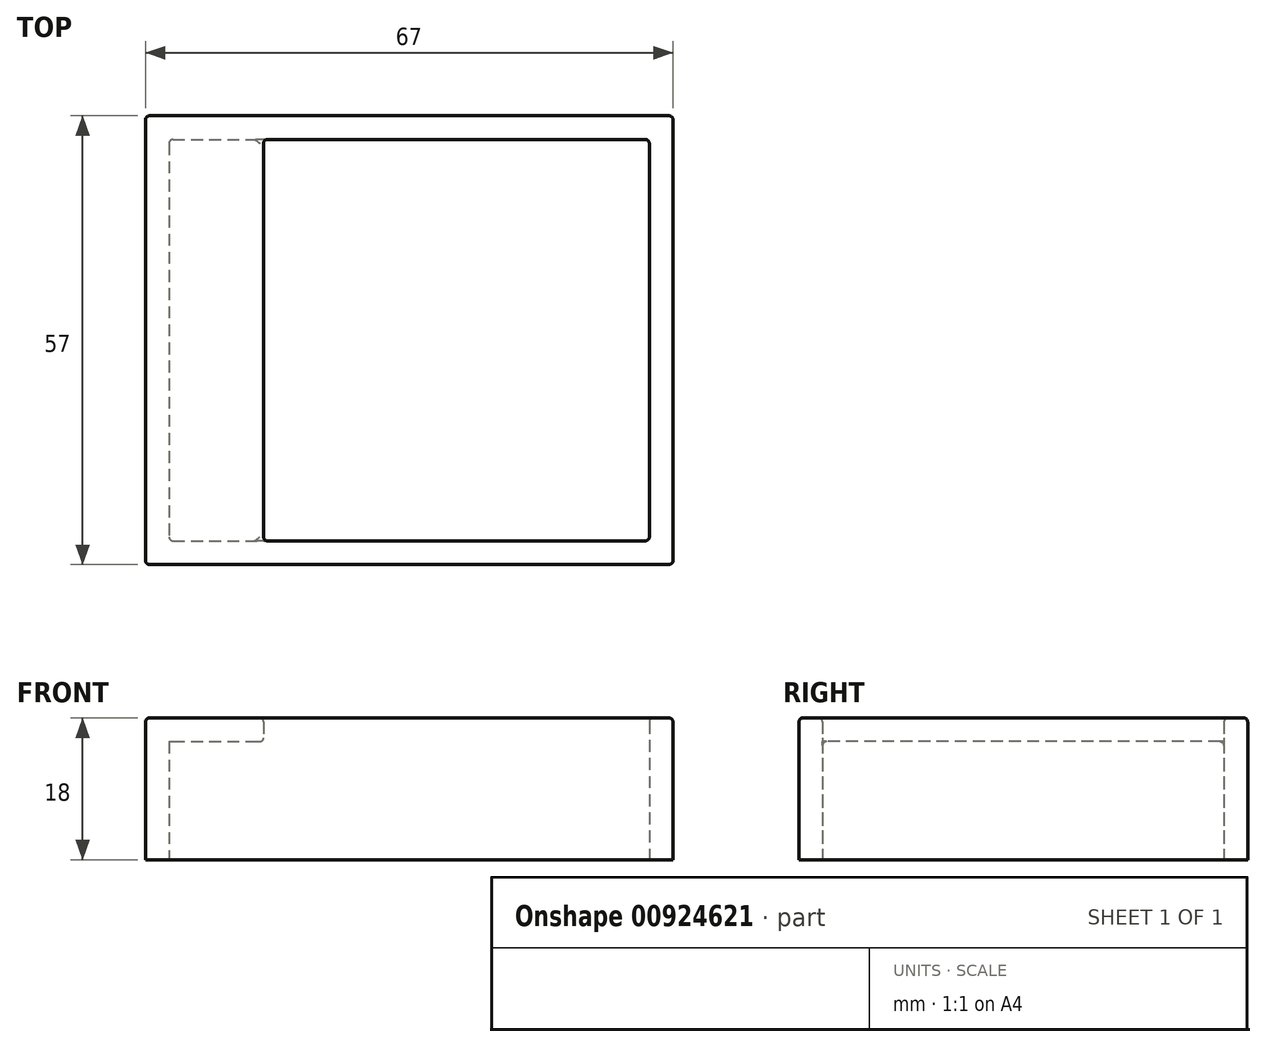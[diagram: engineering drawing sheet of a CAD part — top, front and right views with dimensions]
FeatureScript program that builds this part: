
annotation { "Feature Type Name" : "Feature", "Feature Type Description" : "" }
export const myFeature = defineFeature(function(context is Context, id is Id, definition is map)
    precondition{}
    {
        {
            var Q0;
            Q0=qCreatedBy(makeId("Top.planeOp"),FACE);
            var sketch = newSketch(context, id + "F0", { "sketchPlane" : qUnion([Q0])});
            skLineSegment(sketch, "E0.bottom", {"start": v(-27.46, 16.96) * mm, "end": v(32.54, 16.96) * mm});
            skLineSegment(sketch, "E0.top", {"start": v(-27.46, -34.04) * mm, "end": v(32.54, -34.04) * mm});
            skLineSegment(sketch, "E0.left", {"start": v(-27.96, 16.46) * mm, "end": v(-27.96, -33.54) * mm});
            skLineSegment(sketch, "E0.right", {"start": v(33.04, 16.46) * mm, "end": v(33.04, -33.54) * mm});
            skLineSegment(sketch, "E1.bottom", {"start": v(-30.46, 19.96) * mm, "end": v(35.54, 19.96) * mm});
            skLineSegment(sketch, "E1.top", {"start": v(-30.46, -37.04) * mm, "end": v(35.54, -37.04) * mm});
            skLineSegment(sketch, "E1.left", {"start": v(-30.96, 19.46) * mm, "end": v(-30.96, -36.54) * mm});
            skLineSegment(sketch, "E1.right", {"start": v(36.04, 19.46) * mm, "end": v(36.04, -36.54) * mm});
            skPoint(sketch, "E2.visualSharp", {"position": v(-27.96, 16.96) * mm});
            skArc(sketch, "E2.filletArc", {"start": v(-27.46, 16.96) * mm, "mid": v(-27.82, 16.81) * mm, "end": v(-27.96, 16.46) * mm});
            skPoint(sketch, "E3.visualSharp", {"position": v(33.04, 16.96) * mm});
            skArc(sketch, "E3.filletArc", {"start": v(33.04, 16.46) * mm, "mid": v(32.9, 16.81) * mm, "end": v(32.54, 16.96) * mm});
            skPoint(sketch, "E4.visualSharp", {"position": v(33.04, -34.04) * mm});
            skArc(sketch, "E4.filletArc", {"start": v(32.54, -34.04) * mm, "mid": v(32.9, -33.9) * mm, "end": v(33.04, -33.54) * mm});
            skPoint(sketch, "E5.visualSharp", {"position": v(-27.96, -34.04) * mm});
            skArc(sketch, "E5.filletArc", {"start": v(-27.96, -33.54) * mm, "mid": v(-27.82, -33.9) * mm, "end": v(-27.46, -34.04) * mm});
            skPoint(sketch, "E6.visualSharp", {"position": v(-30.96, 19.96) * mm});
            skArc(sketch, "E6.filletArc", {"start": v(-30.46, 19.96) * mm, "mid": v(-30.82, 19.81) * mm, "end": v(-30.96, 19.46) * mm});
            skPoint(sketch, "E7.visualSharp", {"position": v(36.04, 19.96) * mm});
            skArc(sketch, "E7.filletArc", {"start": v(36.04, 19.46) * mm, "mid": v(35.9, 19.81) * mm, "end": v(35.54, 19.96) * mm});
            skPoint(sketch, "E8.visualSharp", {"position": v(36.04, -37.04) * mm});
            skArc(sketch, "E8.filletArc", {"start": v(35.54, -37.04) * mm, "mid": v(35.9, -36.9) * mm, "end": v(36.04, -36.54) * mm});
            skPoint(sketch, "E9.visualSharp", {"position": v(-30.96, -37.04) * mm});
            skArc(sketch, "E9.filletArc", {"start": v(-30.96, -36.54) * mm, "mid": v(-30.82, -36.9) * mm, "end": v(-30.46, -37.04) * mm});
            skSolve(sketch);
        }
        {
            var Q0;
            Q0=makeQuery(id+"F0.imprint","IMPRINT",FACE,{"disambiguationData":[TD([[makeQuery(id+"F0.imprint","IMPRINT",EDGE,{"derivedFrom":sQuery(id+"F0.wireOp",EDGE,"E0.bottom")}),1.0]])]});
            extrude(context, id + "F1", {"entities" : qUnion([Q0]), "depth" : 15 * mm, "offsetDistance" : 25 * mm});
        }
        {
            var Q0;
            Q0=makeQuery(id+"F1.opExtrude","CAP_FACE",FACE,{"disambiguationData":[OSD([sQuery(id+"F0.wireOp",EDGE,"E0.bottom"),sQuery(id+"F0.wireOp",EDGE,"E0.top"),sQuery(id+"F0.wireOp",EDGE,"E0.left"),sQuery(id+"F0.wireOp",EDGE,"E0.right"),sQuery(id+"F0.wireOp",EDGE,"E1.bottom"),sQuery(id+"F0.wireOp",EDGE,"E1.top"),sQuery(id+"F0.wireOp",EDGE,"E1.left"),sQuery(id+"F0.wireOp",EDGE,"E1.right"),sQuery(id+"F0.wireOp",EDGE,"E2.filletArc"),sQuery(id+"F0.wireOp",EDGE,"E3.filletArc"),sQuery(id+"F0.wireOp",EDGE,"E4.filletArc"),sQuery(id+"F0.wireOp",EDGE,"E5.filletArc"),sQuery(id+"F0.wireOp",EDGE,"E6.filletArc"),sQuery(id+"F0.wireOp",EDGE,"E7.filletArc"),sQuery(id+"F0.wireOp",EDGE,"E8.filletArc"),sQuery(id+"F0.wireOp",EDGE,"E9.filletArc")])],"isStart":false});
            var sketch = newSketch(context, id + "F2", { "sketchPlane" : qUnion([Q0])});
            skLineSegment(sketch, "E10.0", {"start": v(-30.96, 19.46) * mm, "end": v(-30.96, -36.54) * mm});
            skArc(sketch, "E11.0", {"start": v(-30.46, 19.96) * mm, "mid": v(-30.82, 19.81) * mm, "end": v(-30.96, 19.46) * mm});
            skLineSegment(sketch, "E12.0", {"start": v(-30.46, 19.96) * mm, "end": v(35.54, 19.96) * mm});
            skLineSegment(sketch, "E13.0", {"start": v(-30.46, -37.04) * mm, "end": v(35.54, -37.04) * mm});
            skArc(sketch, "E14.0", {"start": v(-30.96, -36.54) * mm, "mid": v(-30.82, -36.9) * mm, "end": v(-30.46, -37.04) * mm});
            skLineSegment(sketch, "E15.0", {"start": v(-27.96, 16.46) * mm, "end": v(-27.96, -33.54) * mm});
            skLineSegment(sketch, "E16", {"start": v(-15.96, 19.96) * mm, "end": v(-15.96, -37.04) * mm});
            skSolve(sketch);
        }
        {
            var Q0;
            Q0=makeQuery(id+"F2.imprint","IMPRINT",FACE,{"disambiguationData":[TD([[makeQuery(id+"F2.imprint","IMPRINT",EDGE,{"derivedFrom":sQuery(id+"F2.wireOp",EDGE,"E15.0")}),1.0]])]});
            var Q1;
            Q1=makeQuery(id+"F2.imprint","IMPRINT",FACE,{"disambiguationData":[TD([[makeQuery(id+"F2.imprint","IMPRINT",EDGE,{"derivedFrom":sQuery(id+"F2.wireOp",EDGE,"E10.0")}),1.0]])]});
            var Q2;
            Q2=makeQuery(id+"F2.imprint","IMPRINT",FACE,{"disambiguationData":[TD([[makeQuery(id+"F2.imprint","IMPRINT",EDGE,{"derivedFrom":makeQuery(id+"F1.opExtrude","CAP_EDGE",EDGE,{"disambiguationData":[OSD([sQuery(id+"F0.wireOp",EDGE,"E0.right")])],"isStart":false})}),1.0]])]});
            extrude(context, id + "F3", {"entities" : qUnion([Q0, Q1, Q2]), "operationType" : NewBodyOperationType.ADD, "depth" : 3 * mm, "offsetDistance" : 25 * mm});
        }
        {
            var Q0;
            Q0=makeQuery(id+"F3.opExtrude","SWEPT_EDGE",EDGE,{"disambiguationData":[OSD([sQuery(id+"F0.wireOp",EDGE,"E0.bottom"),sQuery(id+"F2.wireOp",EDGE,"E16")])]});
            var Q1;
            Q1=makeQuery(id+"F3.opExtrude","SWEPT_EDGE",EDGE,{"disambiguationData":[OSD([sQuery(id+"F0.wireOp",EDGE,"E0.top"),sQuery(id+"F2.wireOp",EDGE,"E16")])]});
            var Q2;
            Q2=makeQuery(id+"F3.opExtrude","CAP_EDGE",EDGE,{"disambiguationData":[OSD([sQuery(id+"F2.wireOp",EDGE,"E16")])],"isStart":false});
            var Q3;
            Q3=makeQuery(id+"F3.opExtrude","CAP_EDGE",EDGE,{"disambiguationData":[OSD([sQuery(id+"F0.wireOp",EDGE,"E0.top")])],"isStart":false});
            var Q4;
            Q4=makeQuery(id+"F3.opExtrude","CAP_EDGE",EDGE,{"disambiguationData":[OSD([sQuery(id+"F2.wireOp",EDGE,"E16")])],"isStart":true});
            var Q5;
            Q5=makeQuery(id+"F3.opExtrude","CAP_EDGE",EDGE,{"disambiguationData":[OSD([sQuery(id+"F2.wireOp",EDGE,"E10.0")])],"isStart":false});
            var Q6;
            Q6=makeQuery(id+"F3.opExtrude","CAP_EDGE",EDGE,{"disambiguationData":[OSD([sQuery(id+"F2.wireOp",EDGE,"E13.0")])],"isStart":false});
            fillet(context, id + "F4", {"entities" : qUnion([Q0, Q1, Q2, Q3, Q4, Q5, Q6]), "radius" : .5 * mm, "tangentPropagation" : true, "allowEdgeOverflow" : false});
        }
    });
